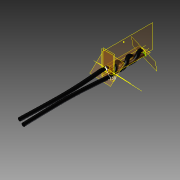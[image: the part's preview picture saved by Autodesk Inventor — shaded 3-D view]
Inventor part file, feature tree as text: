
AUTODESK INVENTOR PART (.ipt)
format: ipt  version: 2014 (Build 180170000, 170)  size: 314,880 bytes
history: native  units: in
note: dims shown in document units (in); Inventor stores cm internally (conversion verified against a paired STEP export)
features: sketch x15, plane x10, other x4, projected_geometry x4, sweep x3, pattern_circular x2, loft x1, reference x1
ambient origin geometry x8: Origin, YZ Plane, XZ Plane, XY Plane, X Axis, Y Axis, Z Axis, Center Point
bodies: Body1 (feature_tree)
feature tree (40):
  sketch  "Sketch1"  dims[d0=1.0in d1=0.5661in d2=0.154in d3=0.0206in d8=0.15in]
  plane  "Work Plane1"
  sketch  "Sketch2"  dims[d9=0.0in d10=0.15in]
  sketch  "3D Sketch1"
  plane  "Work Plane2"
  plane  "Work Plane3"
  sketch  "Sketch3"  dims[d11=0.0625in d16=0.0in]
  other  "Work Axis1"
  plane  "Work Plane5"
  plane  "Work Plane4"
  sketch  "Sketch5"  dims[d17=0.0in d18=0.7874in d19=360.0deg]
  sweep  "Sweep2"
  sketch  "Sketch7"  dims[d26=0.0in d27=90.0deg]
  plane  "Work Plane7"
  sketch  "Sketch8"  dims[d28=0.0in d29=90.0deg]
  plane  "Work Plane8"
  sketch  "Sketch9"  dims[d30=0.0in d31=0.7874in d32=360.0deg]
  other  "Work Axis2"
  plane  "Work Plane9"
  plane  "Work Plane10"
  loft  "Loft2"
  sweep  "Sweep4"
  pattern_circular  "Circular Pattern3"  Count=2 Angle=360.0deg
  sweep  "Sweep3"
  pattern_circular  "Circular Pattern2"  Count=2 Angle=360.0deg
  reference  "Reference1"
  other  "Helical Curve1"
  sketch  "Sketch6"  dims[d23=0.15in d24=0.0in d25=90.0deg]
  projected_geometry  "Projected Loop2"
  plane  "Work Plane6"
  sketch  "Sketch10"
  projected_geometry  "Projected Loop3"
  sketch  "Sketch11"
  sketch  "Sketch12"
  sketch  "Sketch13"
  other  "Edges2"
  sketch  "Sketch14"
  projected_geometry  "Projected Loop5"
  sketch  "Sketch15"
  projected_geometry  "Projected Loop6"
